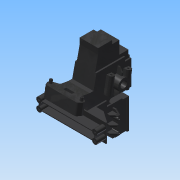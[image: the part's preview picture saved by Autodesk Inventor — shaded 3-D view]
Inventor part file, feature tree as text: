
AUTODESK INVENTOR PART (.ipt)
format: ipt  version: 2014 (Build 180170000, 170)  size: 585,216 bytes
history: native  units: in
note: dims shown in document units (in); Inventor stores cm internally (conversion verified against a paired STEP export)
features: extrude x15, sketch x15, mirror x5, plane x3, chamfer x2, other x1, projected_geometry x1
ambient origin geometry x8: Origin, YZ Plane, XZ Plane, XY Plane, X Axis, Y Axis, Z Axis, Center Point
bodies: Solid1 (feature_tree)
feature tree (42):
  extrude  "Extrusion1"  Depth=1.05in
  extrude  "Extrusion2"  Depth=1.15in
  extrude  "Extrusion3"  Depth=1.42in
  sketch  "Sketch4"  dims[d9=2.0in d10=0.43in]
  mirror  "Mirror1"
  extrude  "Extrusion4"  Depth=0.43in
  sketch  "Sketch5"  dims[d11=0.4in d12=0.97in]
  extrude  "Extrusion5"  Depth=0.97in
  extrude  "Extrusion6"  Depth=0.52in
  chamfer  "Chamfer1"  Distance=1.3in
  mirror  "Mirror2"
  extrude  "Extrusion7"  Depth=0.3in
  extrude  "Extrusion8"  Depth=0.43in
  chamfer  "Chamfer2"  Distance=0.1in
  extrude  "Extrusion9"  Depth=0.4in
  plane  "Work Plane2"
  mirror  "Mirror3"
  mirror  "Mirror4"
  plane  "Work Plane3"
  extrude  "Extrusion10"  Depth=0.372in
  extrude  "Extrusion11"  Depth=0.1in TaperAngle=0.0deg
  extrude  "Extrusion12"  Depth=0.1in TaperAngle=0.0deg
  extrude  "Extrusion13"  Depth=0.125in
  extrude  "Extrusion14"  Depth=0.125in
  mirror  "Mirror5"
  sketch  "Sketch15"  dims[d27=0.15in d28=0.3in d29=0.43in d30=0.1in d31=0.0in d32=0.4in d33=0.372in d34=0.1in d35=0.0in d36=0.1in d37=0.0in d38=0.125in d40=0.125in d41=0.4in d42=0.1in d43=0.0in d44=0.1in d47=0.1in d49=0.17in d51=0.24in d52=0.1in d53=0.32in d54=0.42in d55=0.51in d56=1.72in d57=0.76in d58=0.17in d59=0.98in d60=0.37in d61=0.45in d62=0.0in d63=0.25in d64=0.125in d65=45.0deg d67=0.82in d69=0.51in d70=0.65in d72=0.46in d73=0.54in d74=0.0in d75=0.0687in d76=0.382in d78=0.26in d79=1.15in d80=0.37in d81=0.1in d82=0.35in d83=0.0in d84=0.25in d85=0.125in d86=45.0deg d87=0.125in d89=0.35in d90=0.0in d92=0.0in d93=0.0687in d94=3.42in d95=90.0deg d96=0.58in d97=0.52in d99=0.69in d101=0.15in d102=0.34in d103=0.18in d104=0.125in d105=0.432in d106=0.238in d108=0.593in d109=0.767in d110=0.0in d111=0.194in d112=0.1in d113=0.215in d114=0.0in d115=4.314in d116=1.29in d117=0.08in d118=0.0in d120=0.5in d121=0.08in d122=0.0in d123=0.1in d124=0.1in d125=0.08in d126=0.0in d129=0.1875in d130=0.175in d131=0.175in d135=0.1875in d137=0.025in d138=0.025in d139=0.125in d140=0.609in d141=0.0in d142=1.0in]
  plane  "Work Plane4"
  extrude  "Extrusion15"  Depth=0.4in
  sketch  "Sketch1"  dims[d0=2.128in d2=1.05in]
  sketch  "Sketch2"  dims[d3=1.08in d4=1.15in]
  sketch  "Sketch3"  dims[d5=0.55in d6=1.42in]
  sketch  "Sketch6"  dims[d13=0.25in d14=0.52in]
  sketch  "Sketch7"  dims[d15=0.9in]
  sketch  "Sketch8"  dims[d18=0.64in]
  sketch  "Sketch9"  dims[d19=0.37in]
  other  "Work Axis2"
  sketch  "Sketch10"  dims[d20=0.1in]
  sketch  "Sketch11"  dims[d21=1.9in]
  sketch  "Sketch12"  dims[d22=1.4in]
  sketch  "Sketch13"  dims[d23=0.29in]
  sketch  "Sketch14"  dims[d24=0.27in d25=1.3in d26=0.0in]
  projected_geometry  "Projected Loop1"
